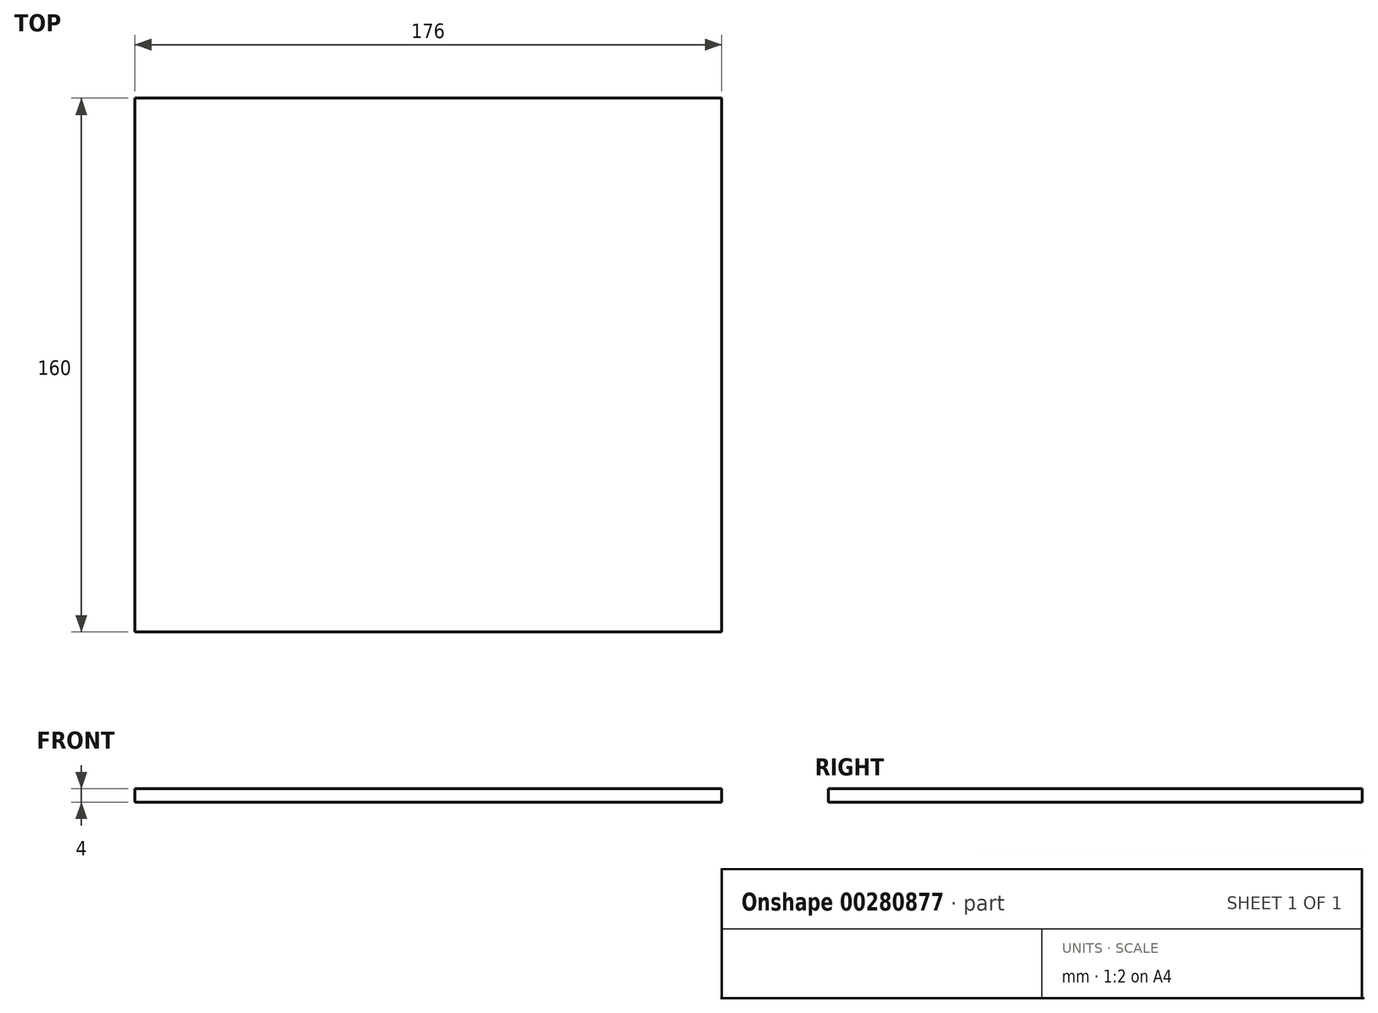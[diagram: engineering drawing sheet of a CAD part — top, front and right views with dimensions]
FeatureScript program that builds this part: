
annotation { "Feature Type Name" : "Feature", "Feature Type Description" : "" }
export const myFeature = defineFeature(function(context is Context, id is Id, definition is map)
    precondition{}
    {
        {
            var Q0;
            Q0=qCreatedBy(makeId("Top.planeOp"),FACE);
            var sketch = newSketch(context, id + "F0", { "sketchPlane" : qUnion([Q0])});
            skLineSegment(sketch, "E0.bottom", {"start": v(-41.22, -30.64) * mm, "end": v(134.78, -30.64) * mm});
            skLineSegment(sketch, "E0.top", {"start": v(-41.22, 129.36) * mm, "end": v(134.78, 129.36) * mm});
            skLineSegment(sketch, "E0.left", {"start": v(-41.22, -30.64) * mm, "end": v(-41.22, 129.36) * mm});
            skLineSegment(sketch, "E0.right", {"start": v(134.78, -30.64) * mm, "end": v(134.78, 129.36) * mm});
            skSolve(sketch);
        }
        {
            var Q0;
            Q0=makeQuery(id+"F0.imprint","IMPRINT",FACE,{"disambiguationData":[TD([[makeQuery(id+"F0.imprint","IMPRINT",EDGE,{"derivedFrom":sQuery(id+"F0.wireOp",EDGE,"E0.bottom")}),1.0]])]});
            extrude(context, id + "F1", {"entities" : qUnion([Q0]), "depth" : 4 * mm});
        }
    });
